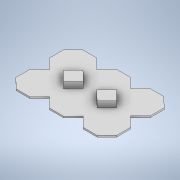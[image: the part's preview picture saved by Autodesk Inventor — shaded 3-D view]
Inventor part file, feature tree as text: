
AUTODESK INVENTOR PART (.ipt)
format: ipt  version: 2020 (Build 240168000, 168)  size: 316,928 bytes
history: native  units: mm
features: extrude x2, sketch x1
ambient origin geometry x8: Origin, YZ Plane, XZ Plane, XY Plane, X Axis, Y Axis, Z Axis, Center Point
bodies: Solid1 (feature_tree)
feature tree (3):
  sketch  "Sketch1"  dims[d0=9.078mm d1=1.0mm d2=0.0mm d3=9.078mm d4=9.078mm d6=5.0mm d7=0.0mm]
  extrude  "Extrusion1"  Depth=1.0mm TaperAngle=0.0deg
  extrude  "Extrusion2"  Depth=9.078mm
